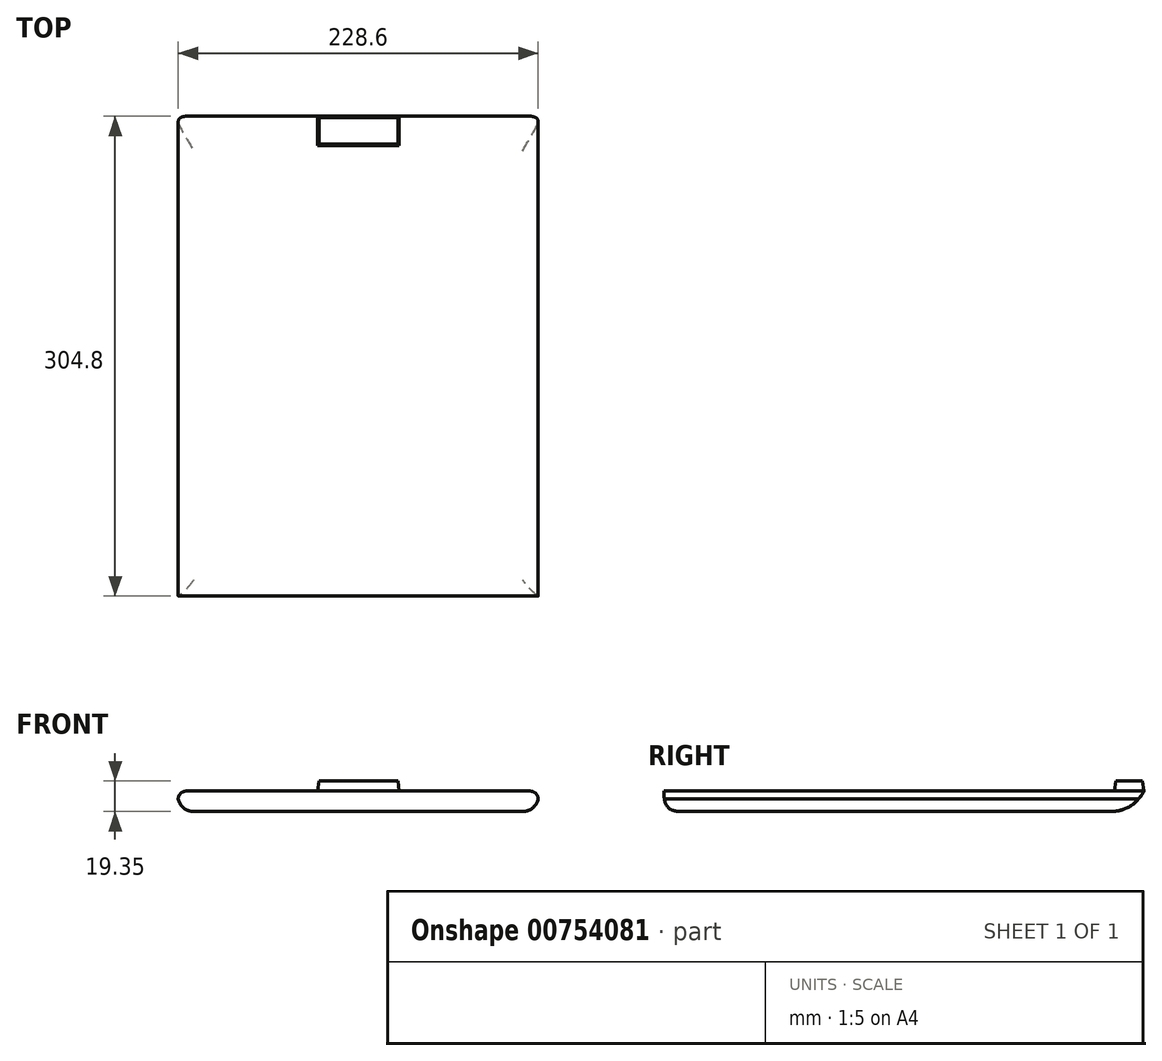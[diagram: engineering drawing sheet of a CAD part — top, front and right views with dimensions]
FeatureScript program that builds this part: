
annotation { "Feature Type Name" : "Feature", "Feature Type Description" : "" }
export const myFeature = defineFeature(function(context is Context, id is Id, definition is map)
    precondition{}
    {
        {
            var Q0;
            Q0=qCreatedBy(makeId("Top.planeOp"),FACE);
            var sketch = newSketch(context, id + "F0", { "sketchPlane" : qUnion([Q0])});
            skLineSegment(sketch, "E0.bottom", {"start": v(114.3, -152.4) * mm, "end": v(-114.3, -152.4) * mm});
            skLineSegment(sketch, "E0.top", {"start": v(114.3, 152.4) * mm, "end": v(-114.3, 152.4) * mm});
            skLineSegment(sketch, "E0.left", {"start": v(114.3, -152.4) * mm, "end": v(114.3, 152.4) * mm});
            skLineSegment(sketch, "E0.right", {"start": v(-114.3, -152.4) * mm, "end": v(-114.3, 152.4) * mm});
            skPoint(sketch, "E0.middle", {"position": v(0, 0) * mm});
            skSolve(sketch);
        }
        {
            var Q0;
            Q0=makeQuery(id+"F0.imprint","IMPRINT",FACE,{"disambiguationData":[TD([[makeQuery(id+"F0.imprint","IMPRINT",EDGE,{"derivedFrom":sQuery(id+"F0.wireOp",EDGE,"E0.bottom")}),-1.0]])]});
            extrude(context, id + "F1", {"entities" : qUnion([Q0]), "depth" : 13 * mm, "offsetDistance" : 25.4 * mm});
        }
        {
            var Q0;
            Q0=makeQuery(id+"F1.opExtrude","CAP_EDGE",EDGE,{"disambiguationData":[OSD([sQuery(id+"F0.wireOp",EDGE,"E0.left")])],"isStart":false});
            var Q1;
            Q1=makeQuery(id+"F1.opExtrude","CAP_EDGE",EDGE,{"disambiguationData":[OSD([sQuery(id+"F0.wireOp",EDGE,"E0.right")])],"isStart":false});
            fillet(context, id + "F2", {"entities" : qUnion([Q0, Q1]), "radius" : 5.08 * mm, "tangentPropagation" : true, "allowEdgeOverflow" : false});
        }
        {
            var Q0;
            Q0=makeQuery(id+"F1.opExtrude","CAP_EDGE",EDGE,{"disambiguationData":[OSD([sQuery(id+"F0.wireOp",EDGE,"E0.left")])],"isStart":true});
            var Q1;
            Q1=makeQuery(id+"F1.opExtrude","CAP_EDGE",EDGE,{"disambiguationData":[OSD([sQuery(id+"F0.wireOp",EDGE,"E0.right")])],"isStart":true});
            fillet(context, id + "F3", {"entities" : qUnion([Q0, Q1]), "radius" : 10.16 * mm, "tangentPropagation" : true, "allowEdgeOverflow" : false});
        }
        {
            var Q0;
            Q0=makeQuery(id+"F1.opExtrude","CAP_EDGE",EDGE,{"disambiguationData":[OSD([sQuery(id+"F0.wireOp",EDGE,"E0.top")])],"isStart":true});
            fillet(context, id + "F4", {"entities" : qUnion([Q0]), "radius" : 25.14 * mm, "tangentPropagation" : true, "rho" : 0.5, "crossSection" : FilletCrossSection.CONIC, "allowEdgeOverflow" : false});
        }
        {
            var Q0;
            Q0=makeQuery(id+"F1.opExtrude","CAP_EDGE",EDGE,{"disambiguationData":[OSD([sQuery(id+"F0.wireOp",EDGE,"E0.bottom")])],"isStart":true});
            fillet(context, id + "F5", {"entities" : qUnion([Q0]), "radius" : 10.42 * mm, "tangentPropagation" : true, "rho" : 0.5, "crossSection" : FilletCrossSection.CONIC, "allowEdgeOverflow" : false});
        }
        {
            var Q0;
            Q0=makeQuery(id+"F1.opExtrude","CAP_FACE",FACE,{"disambiguationData":[OSD([sQuery(id+"F0.wireOp",EDGE,"E0.bottom"),sQuery(id+"F0.wireOp",EDGE,"E0.top"),sQuery(id+"F0.wireOp",EDGE,"E0.left"),sQuery(id+"F0.wireOp",EDGE,"E0.right")])],"isStart":false});
            var sketch = newSketch(context, id + "F6", { "sketchPlane" : qUnion([Q0])});
            skLineSegment(sketch, "E1.bottom", {"start": v(-25.83, 152.4) * mm, "end": v(26.09, 152.4) * mm});
            skLineSegment(sketch, "E1.top", {"start": v(-25.83, 133.73) * mm, "end": v(26.09, 133.73) * mm});
            skLineSegment(sketch, "E1.left", {"start": v(-25.83, 152.4) * mm, "end": v(-25.83, 133.73) * mm});
            skLineSegment(sketch, "E1.right", {"start": v(26.09, 152.4) * mm, "end": v(26.09, 133.73) * mm});
            skSolve(sketch);
        }
        {
            var Q0;
            Q0=makeQuery(id+"F6.imprint","IMPRINT",FACE,{"disambiguationData":[TD([[makeQuery(id+"F6.imprint","IMPRINT",EDGE,{"derivedFrom":sQuery(id+"F6.wireOp",EDGE,"E1.bottom")}),1.0]])]});
            extrude(context, id + "F7", {"entities" : qUnion([Q0]), "operationType" : NewBodyOperationType.ADD, "depth" : 6.35 * mm, "offsetDistance" : 25.4 * mm, "hasDraft" : true, "draftAngle" : 8 * degree, "draftPullDirection" : true});
        }
    });
